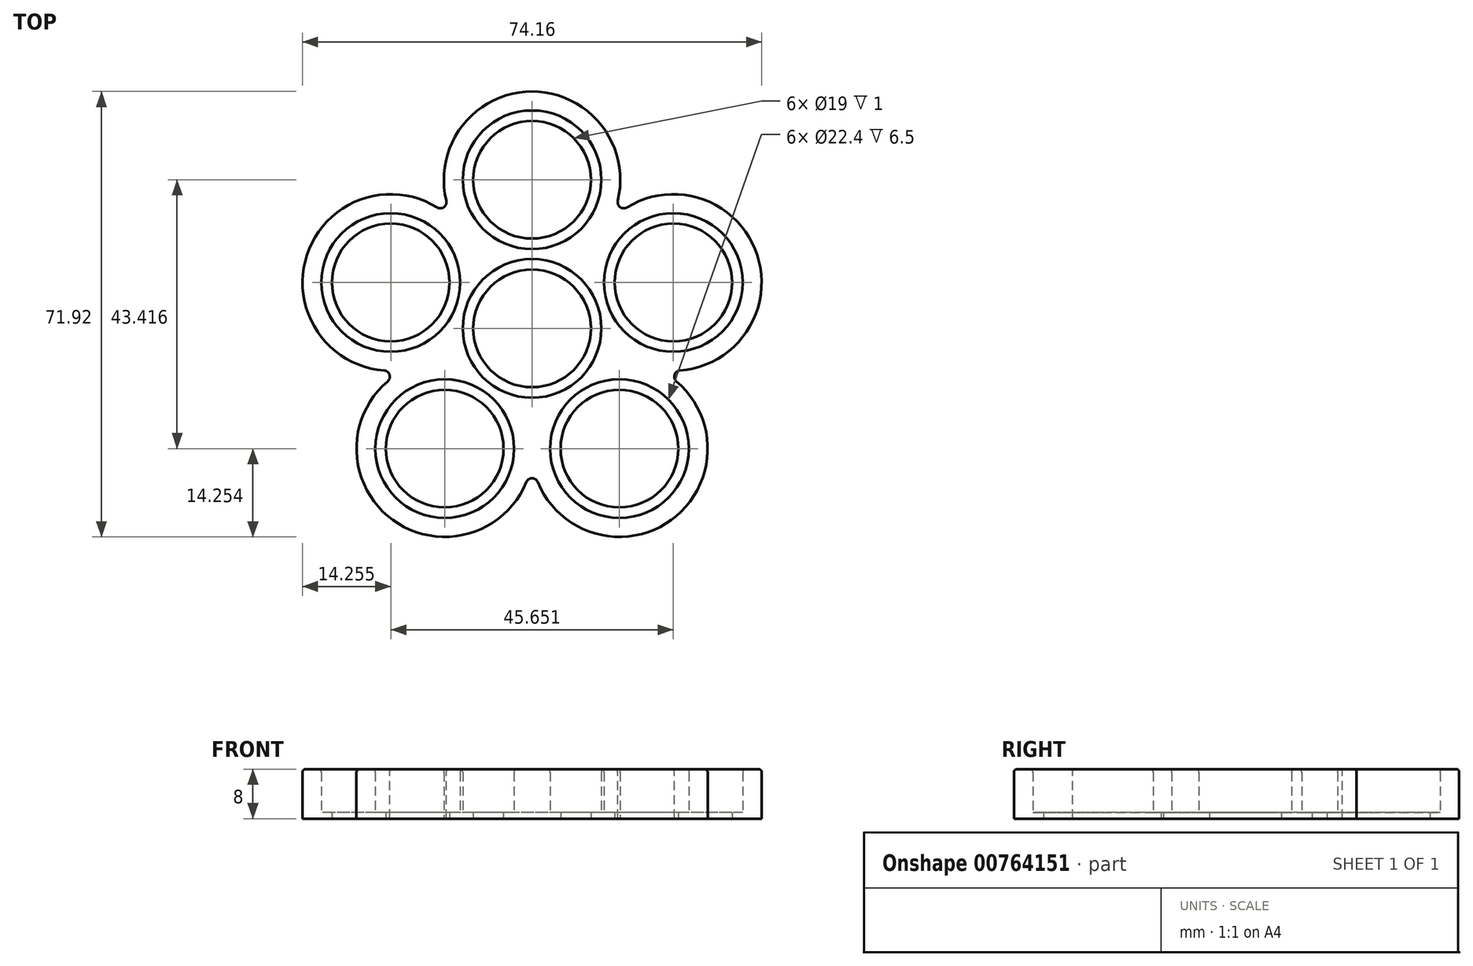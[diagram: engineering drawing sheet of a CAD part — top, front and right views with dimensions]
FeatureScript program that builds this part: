
annotation { "Feature Type Name" : "Feature", "Feature Type Description" : "" }
export const myFeature = defineFeature(function(context is Context, id is Id, definition is map)
    precondition{}
    {
        {
            var Q0;
            Q0=qCreatedBy(makeId("Top.planeOp"),FACE);
            var sketch = newSketch(context, id + "F0", { "sketchPlane" : qUnion([Q0])});
            skCircle(sketch, "E0", {"center": v(0, 0) * mm, "radius": 11.2 * mm});
            skCircle(sketch, "E1", {"center": v(0, 0) * mm, "radius": 14 * mm});
            skCircle(sketch, "E2", {"center": v(0, 24) * mm, "radius": 11.2 * mm});
            skCircle(sketch, "E3", {"center": v(0, 24) * mm, "radius": 14.25 * mm});
            skLineSegment(sketch, "E4", {"start": v(0, 24) * mm, "end": v(0, 0) * mm, "construction": true});
            skCircle(sketch, "E5", {"center": v(0, 24) * mm, "radius": 9.5 * mm});
            skCircle(sketch, "E6", {"center": v(0, 0) * mm, "radius": 9.5 * mm});
            skLineSegment(sketch, "E7.1.0", {"start": v(-22.83, 7.42) * mm, "end": v(0, 0) * mm, "construction": true});
            skCircle(sketch, "E7.1.1", {"center": v(-22.83, 7.42) * mm, "radius": 9.5 * mm});
            skCircle(sketch, "E7.1.2", {"center": v(-22.83, 7.42) * mm, "radius": 11.2 * mm});
            skCircle(sketch, "E7.1.3", {"center": v(-22.83, 7.42) * mm, "radius": 14.25 * mm});
            skLineSegment(sketch, "E7.2.0", {"start": v(-14.1, -19.42) * mm, "end": v(0, 0) * mm, "construction": true});
            skCircle(sketch, "E7.2.1", {"center": v(-14.1, -19.42) * mm, "radius": 9.5 * mm});
            skCircle(sketch, "E7.2.2", {"center": v(-14.1, -19.42) * mm, "radius": 11.2 * mm});
            skCircle(sketch, "E7.2.3", {"center": v(-14.1, -19.42) * mm, "radius": 14.25 * mm});
            skLineSegment(sketch, "E7.3.0", {"start": v(14.1, -19.42) * mm, "end": v(0, 0) * mm, "construction": true});
            skCircle(sketch, "E7.3.1", {"center": v(14.1, -19.42) * mm, "radius": 9.5 * mm});
            skCircle(sketch, "E7.3.2", {"center": v(14.1, -19.42) * mm, "radius": 11.2 * mm});
            skCircle(sketch, "E7.3.3", {"center": v(14.1, -19.42) * mm, "radius": 14.25 * mm});
            skLineSegment(sketch, "E7.4.0", {"start": v(22.83, 7.42) * mm, "end": v(0, 0) * mm, "construction": true});
            skCircle(sketch, "E7.4.1", {"center": v(22.83, 7.42) * mm, "radius": 9.5 * mm});
            skCircle(sketch, "E7.4.2", {"center": v(22.83, 7.42) * mm, "radius": 11.2 * mm});
            skCircle(sketch, "E7.4.3", {"center": v(22.83, 7.42) * mm, "radius": 14.25 * mm});
            skSolve(sketch);
        }
        {
            var Q0;
            Q0=qSketchRegion(id+"F0",true);
            var Q1;
            Q1=makeQuery(id+"F0.imprint","IMPRINT",FACE,{"disambiguationData":[TD([[makeQuery(id+"F0.imprint","IMPRINT",EDGE,{"derivedFrom":sQuery(id+"F0.wireOp",EDGE,"E0")}),1.0]])]});
            var Q2;
            {var subQ0=sQuery(id+"F0.wireOp",EDGE,"E2");var subQ1=sQuery(id+"F0.wireOp",EDGE,"E1");var subQ2=makeQuery(id+"F0.imprint","INTERSECT",VERTEX,{"disambiguationData":[OD(0.0)],"derivedFrom":[subQ1,subQ0]});Q2=makeQuery(id+"F0.imprint","IMPRINT",FACE,{"disambiguationData":[TD([[makeQuery(id+"F0.imprint","IMPRINT",EDGE,{"disambiguationData":[TD([[subQ2,-1.0]])],"derivedFrom":subQ1}),1.0]])]});}
            var Q3;
            {var subQ0=sQuery(id+"F0.wireOp",EDGE,"E2");var subQ1=sQuery(id+"F0.wireOp",EDGE,"E1");var subQ2=makeQuery(id+"F0.imprint","INTERSECT",VERTEX,{"disambiguationData":[OD(0.0)],"derivedFrom":[subQ1,subQ0]});Q3=makeQuery(id+"F0.imprint","IMPRINT",FACE,{"disambiguationData":[TD([[makeQuery(id+"F0.imprint","IMPRINT",EDGE,{"disambiguationData":[TD([[subQ2,-1.0]])],"derivedFrom":subQ1}),-1.0]])]});}
            var Q4;
            {var subQ0=sQuery(id+"F0.wireOp",EDGE,"MJdSrlI8-rVfH-V2LY-VGwR-c2a5gXK0sPas");var subQ1=sQuery(id+"F0.wireOp",EDGE,"E1");var subQ2=makeQuery(id+"F0.imprint","INTERSECT",VERTEX,{"disambiguationData":[OD(0.0)],"derivedFrom":[subQ1,subQ0]});Q4=makeQuery(id+"F0.imprint","IMPRINT",FACE,{"disambiguationData":[TD([[makeQuery(id+"F0.imprint","IMPRINT",EDGE,{"disambiguationData":[TD([[subQ2,-1.0]])],"derivedFrom":subQ1}),1.0]])]});}
            var Q5;
            {var subQ0=sQuery(id+"F0.wireOp",EDGE,"MJdSrlI8-rVfH-V2LY-VGwR-c2a5gXK0sPas");var subQ1=sQuery(id+"F0.wireOp",EDGE,"E1");var subQ2=makeQuery(id+"F0.imprint","INTERSECT",VERTEX,{"disambiguationData":[OD(0.0)],"derivedFrom":[subQ1,subQ0]});Q5=makeQuery(id+"F0.imprint","IMPRINT",FACE,{"disambiguationData":[TD([[makeQuery(id+"F0.imprint","IMPRINT",EDGE,{"disambiguationData":[TD([[subQ2,-1.0]])],"derivedFrom":subQ1}),-1.0]])]});}
            var Q6;
            {var subQ0=sQuery(id+"F0.wireOp",EDGE,"zHFCQELd-Fm6N-4mPB-3y46-Qqn4AbVFevso");var subQ1=sQuery(id+"F0.wireOp",EDGE,"E1");var subQ2=makeQuery(id+"F0.imprint","INTERSECT",VERTEX,{"disambiguationData":[OD(0.0)],"derivedFrom":[subQ1,subQ0]});Q6=makeQuery(id+"F0.imprint","IMPRINT",FACE,{"disambiguationData":[TD([[makeQuery(id+"F0.imprint","IMPRINT",EDGE,{"disambiguationData":[TD([[subQ2,-1.0]])],"derivedFrom":subQ1}),1.0]])]});}
            var Q7;
            {var subQ0=sQuery(id+"F0.wireOp",EDGE,"zHFCQELd-Fm6N-4mPB-3y46-Qqn4AbVFevso");var subQ1=sQuery(id+"F0.wireOp",EDGE,"E1");var subQ2=makeQuery(id+"F0.imprint","INTERSECT",VERTEX,{"disambiguationData":[OD(0.0)],"derivedFrom":[subQ1,subQ0]});Q7=makeQuery(id+"F0.imprint","IMPRINT",FACE,{"disambiguationData":[TD([[makeQuery(id+"F0.imprint","IMPRINT",EDGE,{"disambiguationData":[TD([[subQ2,-1.0]])],"derivedFrom":subQ1}),-1.0]])]});}
            var Q8;
            {var subQ0=sQuery(id+"F0.wireOp",EDGE,"owKKNgS1-acpY-2382-gatt-TBliOJCZXLt6");var subQ1=sQuery(id+"F0.wireOp",EDGE,"E0");var subQ2=makeQuery(id+"F0.imprint","INTERSECT",VERTEX,{"disambiguationData":[OD(0.0)],"derivedFrom":[subQ1,subQ0]});Q8=makeQuery(id+"F0.imprint","IMPRINT",FACE,{"disambiguationData":[TD([[makeQuery(id+"F0.imprint","IMPRINT",EDGE,{"disambiguationData":[TD([[subQ2,-1.0]])],"derivedFrom":subQ1}),1.0]])]});}
            var Q9;
            {var subQ0=sQuery(id+"F0.wireOp",EDGE,"aMbKunLI-uIGq-Xlfk-LzCX-02N4p1kP5Les");var subQ1=sQuery(id+"F0.wireOp",EDGE,"E0");var subQ2=makeQuery(id+"F0.imprint","INTERSECT",VERTEX,{"disambiguationData":[OD(0.0)],"derivedFrom":[subQ1,subQ0]});Q9=makeQuery(id+"F0.imprint","IMPRINT",FACE,{"disambiguationData":[TD([[makeQuery(id+"F0.imprint","IMPRINT",EDGE,{"disambiguationData":[TD([[subQ2,-1.0]])],"derivedFrom":subQ1}),1.0]])]});}
            var Q10;
            {var subQ0=sQuery(id+"F0.wireOp",EDGE,"E3");var subQ1=sQuery(id+"F0.wireOp",EDGE,"E0");var subQ2=makeQuery(id+"F0.imprint","INTERSECT",VERTEX,{"disambiguationData":[OD(0.0)],"derivedFrom":[subQ1,subQ0]});Q10=makeQuery(id+"F0.imprint","IMPRINT",FACE,{"disambiguationData":[TD([[makeQuery(id+"F0.imprint","IMPRINT",EDGE,{"disambiguationData":[TD([[subQ2,1.0]])],"derivedFrom":subQ1}),1.0]])]});}
            var Q11;
            {var subQ4=sQuery(id+"F0.wireOp",EDGE,"E3");var subQ7=sQuery(id+"F0.wireOp",EDGE,"E0");var subQ8=makeQuery(id+"F0.imprint","INTERSECT",VERTEX,{"disambiguationData":[OD(0.0)],"derivedFrom":[subQ7,subQ4]});Q11=makeQuery(id+"F0.imprint","IMPRINT",FACE,{"disambiguationData":[TD([[makeQuery(id+"F0.imprint","IMPRINT",EDGE,{"disambiguationData":[TD([[subQ8,-1.0]])],"derivedFrom":subQ7}),-1.0]])]});}
            var Q12;
            {var subQ0=sQuery(id+"F0.wireOp",EDGE,"E3");var subQ1=sQuery(id+"F0.wireOp",EDGE,"E0");var subQ2=makeQuery(id+"F0.imprint","INTERSECT",VERTEX,{"disambiguationData":[OD(0.0)],"derivedFrom":[subQ1,subQ0]});Q12=makeQuery(id+"F0.imprint","IMPRINT",FACE,{"disambiguationData":[TD([[makeQuery(id+"F0.imprint","IMPRINT",EDGE,{"disambiguationData":[TD([[subQ2,-1.0]])],"derivedFrom":subQ1}),1.0]])]});}
            var Q13;
            Q13=makeQuery(id+"F0.imprint","IMPRINT",FACE,{"disambiguationData":[TD([[makeQuery(id+"F0.imprint","IMPRINT",EDGE,{"derivedFrom":sQuery(id+"F0.wireOp",EDGE,"E7.1.1")}),-1.0]])]});
            var Q14;
            Q14=makeQuery(id+"F0.imprint","IMPRINT",FACE,{"disambiguationData":[TD([[makeQuery(id+"F0.imprint","IMPRINT",EDGE,{"derivedFrom":sQuery(id+"F0.wireOp",EDGE,"E7.4.1")}),-1.0]])]});
            var Q15;
            Q15=makeQuery(id+"F0.imprint","IMPRINT",FACE,{"disambiguationData":[TD([[makeQuery(id+"F0.imprint","IMPRINT",EDGE,{"derivedFrom":sQuery(id+"F0.wireOp",EDGE,"E7.3.1")}),-1.0]])]});
            var Q16;
            Q16=makeQuery(id+"F0.imprint","IMPRINT",FACE,{"disambiguationData":[TD([[makeQuery(id+"F0.imprint","IMPRINT",EDGE,{"derivedFrom":sQuery(id+"F0.wireOp",EDGE,"E7.2.1")}),-1.0]])]});
            var Q17;
            {var subQ0=sQuery(id+"F0.wireOp",EDGE,"E7.1.3");var subQ1=sQuery(id+"F0.wireOp",EDGE,"E1");var subQ2=makeQuery(id+"F0.imprint","INTERSECT",VERTEX,{"disambiguationData":[OD(1.0)],"derivedFrom":[subQ1,subQ0]});Q17=makeQuery(id+"F0.imprint","IMPRINT",FACE,{"disambiguationData":[TD([[makeQuery(id+"F0.imprint","IMPRINT",EDGE,{"disambiguationData":[TD([[subQ2,-1.0]])],"derivedFrom":subQ1}),-1.0]])]});}
            var Q18;
            {var subQ0=sQuery(id+"F0.wireOp",EDGE,"E7.1.3");var subQ1=sQuery(id+"F0.wireOp",EDGE,"E0");var subQ2=makeQuery(id+"F0.imprint","INTERSECT",VERTEX,{"disambiguationData":[OD(1.0)],"derivedFrom":[subQ1,subQ0]});Q18=makeQuery(id+"F0.imprint","IMPRINT",FACE,{"disambiguationData":[TD([[makeQuery(id+"F0.imprint","IMPRINT",EDGE,{"disambiguationData":[TD([[subQ2,-1.0]])],"derivedFrom":subQ1}),-1.0]])]});}
            var Q19;
            {var subQ4=sQuery(id+"F0.wireOp",EDGE,"E7.2.3");var subQ7=sQuery(id+"F0.wireOp",EDGE,"E0");var subQ8=makeQuery(id+"F0.imprint","INTERSECT",VERTEX,{"disambiguationData":[OD(0.0)],"derivedFrom":[subQ7,subQ4]});Q19=makeQuery(id+"F0.imprint","IMPRINT",FACE,{"disambiguationData":[TD([[makeQuery(id+"F0.imprint","IMPRINT",EDGE,{"disambiguationData":[TD([[subQ8,-1.0]])],"derivedFrom":subQ7}),-1.0]])]});}
            var Q20;
            {var subQ0=sQuery(id+"F0.wireOp",EDGE,"E7.2.2");var subQ1=sQuery(id+"F0.wireOp",EDGE,"E1");var subQ2=makeQuery(id+"F0.imprint","INTERSECT",VERTEX,{"disambiguationData":[OD(0.0)],"derivedFrom":[subQ1,subQ0]});Q20=makeQuery(id+"F0.imprint","IMPRINT",FACE,{"disambiguationData":[TD([[makeQuery(id+"F0.imprint","IMPRINT",EDGE,{"disambiguationData":[TD([[subQ2,-1.0]])],"derivedFrom":subQ1}),1.0]])]});}
            var Q21;
            {var subQ0=sQuery(id+"F0.wireOp",EDGE,"E7.2.3");var subQ1=sQuery(id+"F0.wireOp",EDGE,"E0");var subQ2=makeQuery(id+"F0.imprint","INTERSECT",VERTEX,{"disambiguationData":[OD(0.0)],"derivedFrom":[subQ1,subQ0]});Q21=makeQuery(id+"F0.imprint","IMPRINT",FACE,{"disambiguationData":[TD([[makeQuery(id+"F0.imprint","IMPRINT",EDGE,{"disambiguationData":[TD([[subQ2,-1.0]])],"derivedFrom":subQ1}),1.0]])]});}
            var Q22;
            {var subQ3=sQuery(id+"F0.wireOp",EDGE,"E7.1.3");var subQ7=sQuery(id+"F0.wireOp",EDGE,"E0");var subQ8=makeQuery(id+"F0.imprint","INTERSECT",VERTEX,{"disambiguationData":[OD(0.0)],"derivedFrom":[subQ7,subQ3]});Q22=makeQuery(id+"F0.imprint","IMPRINT",FACE,{"disambiguationData":[TD([[makeQuery(id+"F0.imprint","IMPRINT",EDGE,{"disambiguationData":[TD([[subQ8,-1.0]])],"derivedFrom":subQ7}),-1.0]])]});}
            var Q23;
            {var subQ0=sQuery(id+"F0.wireOp",EDGE,"E7.1.2");var subQ1=sQuery(id+"F0.wireOp",EDGE,"E1");var subQ2=makeQuery(id+"F0.imprint","INTERSECT",VERTEX,{"disambiguationData":[OD(0.0)],"derivedFrom":[subQ1,subQ0]});Q23=makeQuery(id+"F0.imprint","IMPRINT",FACE,{"disambiguationData":[TD([[makeQuery(id+"F0.imprint","IMPRINT",EDGE,{"disambiguationData":[TD([[subQ2,-1.0]])],"derivedFrom":subQ1}),1.0]])]});}
            var Q24;
            {var subQ0=sQuery(id+"F0.wireOp",EDGE,"E7.1.3");var subQ1=sQuery(id+"F0.wireOp",EDGE,"E0");var subQ2=makeQuery(id+"F0.imprint","INTERSECT",VERTEX,{"disambiguationData":[OD(0.0)],"derivedFrom":[subQ1,subQ0]});Q24=makeQuery(id+"F0.imprint","IMPRINT",FACE,{"disambiguationData":[TD([[makeQuery(id+"F0.imprint","IMPRINT",EDGE,{"disambiguationData":[TD([[subQ2,-1.0]])],"derivedFrom":subQ1}),1.0]])]});}
            var Q25;
            {var subQ0=sQuery(id+"F0.wireOp",EDGE,"E3");var subQ1=sQuery(id+"F0.wireOp",EDGE,"E0");var subQ2=makeQuery(id+"F0.imprint","INTERSECT",VERTEX,{"disambiguationData":[OD(1.0)],"derivedFrom":[subQ1,subQ0]});Q25=makeQuery(id+"F0.imprint","IMPRINT",FACE,{"disambiguationData":[TD([[makeQuery(id+"F0.imprint","IMPRINT",EDGE,{"disambiguationData":[TD([[subQ2,-1.0]])],"derivedFrom":subQ1}),-1.0]])]});}
            var Q26;
            {var subQ0=sQuery(id+"F0.wireOp",EDGE,"E3");var subQ1=sQuery(id+"F0.wireOp",EDGE,"E1");var subQ2=makeQuery(id+"F0.imprint","INTERSECT",VERTEX,{"disambiguationData":[OD(1.0)],"derivedFrom":[subQ1,subQ0]});Q26=makeQuery(id+"F0.imprint","IMPRINT",FACE,{"disambiguationData":[TD([[makeQuery(id+"F0.imprint","IMPRINT",EDGE,{"disambiguationData":[TD([[subQ2,-1.0]])],"derivedFrom":subQ1}),-1.0]])]});}
            var Q27;
            {var subQ0=sQuery(id+"F0.wireOp",EDGE,"E3");var subQ1=sQuery(id+"F0.wireOp",EDGE,"E0");var subQ2=makeQuery(id+"F0.imprint","INTERSECT",VERTEX,{"disambiguationData":[OD(0.0)],"derivedFrom":[subQ1,subQ0]});Q27=makeQuery(id+"F0.imprint","IMPRINT",FACE,{"disambiguationData":[TD([[makeQuery(id+"F0.imprint","IMPRINT",EDGE,{"disambiguationData":[TD([[subQ2,1.0]])],"derivedFrom":subQ1}),-1.0]])]});}
            var Q28;
            {var subQ0=sQuery(id+"F0.wireOp",EDGE,"E7.4.3");var subQ1=sQuery(id+"F0.wireOp",EDGE,"E1");var subQ2=makeQuery(id+"F0.imprint","INTERSECT",VERTEX,{"disambiguationData":[OD(0.0)],"derivedFrom":[subQ1,subQ0]});Q28=makeQuery(id+"F0.imprint","IMPRINT",FACE,{"disambiguationData":[TD([[makeQuery(id+"F0.imprint","IMPRINT",EDGE,{"disambiguationData":[TD([[subQ2,-1.0]])],"derivedFrom":subQ1}),-1.0]])]});}
            var Q29;
            {var subQ4=sQuery(id+"F0.wireOp",EDGE,"E7.4.3");var subQ7=sQuery(id+"F0.wireOp",EDGE,"E0");var subQ8=makeQuery(id+"F0.imprint","INTERSECT",VERTEX,{"disambiguationData":[OD(0.0)],"derivedFrom":[subQ7,subQ4]});Q29=makeQuery(id+"F0.imprint","IMPRINT",FACE,{"disambiguationData":[TD([[makeQuery(id+"F0.imprint","IMPRINT",EDGE,{"disambiguationData":[TD([[subQ8,1.0]])],"derivedFrom":subQ7}),-1.0]])]});}
            var Q30;
            {var subQ0=sQuery(id+"F0.wireOp",EDGE,"E7.4.2");var subQ1=sQuery(id+"F0.wireOp",EDGE,"E1");var subQ2=makeQuery(id+"F0.imprint","INTERSECT",VERTEX,{"disambiguationData":[OD(0.0)],"derivedFrom":[subQ1,subQ0]});Q30=makeQuery(id+"F0.imprint","IMPRINT",FACE,{"disambiguationData":[TD([[makeQuery(id+"F0.imprint","IMPRINT",EDGE,{"disambiguationData":[TD([[subQ2,1.0]])],"derivedFrom":subQ1}),1.0]])]});}
            var Q31;
            {var subQ0=sQuery(id+"F0.wireOp",EDGE,"E7.4.3");var subQ1=sQuery(id+"F0.wireOp",EDGE,"E0");var subQ2=makeQuery(id+"F0.imprint","INTERSECT",VERTEX,{"disambiguationData":[OD(0.0)],"derivedFrom":[subQ1,subQ0]});Q31=makeQuery(id+"F0.imprint","IMPRINT",FACE,{"disambiguationData":[TD([[makeQuery(id+"F0.imprint","IMPRINT",EDGE,{"disambiguationData":[TD([[subQ2,1.0]])],"derivedFrom":subQ1}),1.0]])]});}
            var Q32;
            {var subQ0=sQuery(id+"F0.wireOp",EDGE,"E7.3.3");var subQ1=sQuery(id+"F0.wireOp",EDGE,"E1");var subQ2=makeQuery(id+"F0.imprint","INTERSECT",VERTEX,{"disambiguationData":[OD(1.0)],"derivedFrom":[subQ1,subQ0]});Q32=makeQuery(id+"F0.imprint","IMPRINT",FACE,{"disambiguationData":[TD([[makeQuery(id+"F0.imprint","IMPRINT",EDGE,{"disambiguationData":[TD([[subQ2,-1.0]])],"derivedFrom":subQ1}),-1.0]])]});}
            var Q33;
            {var subQ0=sQuery(id+"F0.wireOp",EDGE,"E7.3.3");var subQ1=sQuery(id+"F0.wireOp",EDGE,"E0");var subQ2=makeQuery(id+"F0.imprint","INTERSECT",VERTEX,{"disambiguationData":[OD(1.0)],"derivedFrom":[subQ1,subQ0]});Q33=makeQuery(id+"F0.imprint","IMPRINT",FACE,{"disambiguationData":[TD([[makeQuery(id+"F0.imprint","IMPRINT",EDGE,{"disambiguationData":[TD([[subQ2,-1.0]])],"derivedFrom":subQ1}),-1.0]])]});}
            var Q34;
            {var subQ4=sQuery(id+"F0.wireOp",EDGE,"E7.3.3");var subQ6=sQuery(id+"F0.wireOp",EDGE,"E0");var subQ9=makeQuery(id+"F0.imprint","INTERSECT",VERTEX,{"disambiguationData":[OD(0.0)],"derivedFrom":[subQ6,subQ4]});Q34=makeQuery(id+"F0.imprint","IMPRINT",FACE,{"disambiguationData":[TD([[makeQuery(id+"F0.imprint","IMPRINT",EDGE,{"disambiguationData":[TD([[subQ9,-1.0]])],"derivedFrom":subQ6}),-1.0]])]});}
            var Q35;
            {var subQ0=sQuery(id+"F0.wireOp",EDGE,"E7.3.3");var subQ1=sQuery(id+"F0.wireOp",EDGE,"E0");var subQ2=makeQuery(id+"F0.imprint","INTERSECT",VERTEX,{"disambiguationData":[OD(0.0)],"derivedFrom":[subQ1,subQ0]});Q35=makeQuery(id+"F0.imprint","IMPRINT",FACE,{"disambiguationData":[TD([[makeQuery(id+"F0.imprint","IMPRINT",EDGE,{"disambiguationData":[TD([[subQ2,-1.0]])],"derivedFrom":subQ1}),1.0]])]});}
            var Q36;
            {var subQ0=sQuery(id+"F0.wireOp",EDGE,"E7.3.2");var subQ1=sQuery(id+"F0.wireOp",EDGE,"E1");var subQ2=makeQuery(id+"F0.imprint","INTERSECT",VERTEX,{"disambiguationData":[OD(0.0)],"derivedFrom":[subQ1,subQ0]});Q36=makeQuery(id+"F0.imprint","IMPRINT",FACE,{"disambiguationData":[TD([[makeQuery(id+"F0.imprint","IMPRINT",EDGE,{"disambiguationData":[TD([[subQ2,-1.0]])],"derivedFrom":subQ1}),1.0]])]});}
            var Q37;
            {var subQ0=sQuery(id+"F0.wireOp",EDGE,"E7.2.3");var subQ1=sQuery(id+"F0.wireOp",EDGE,"E0");var subQ2=makeQuery(id+"F0.imprint","INTERSECT",VERTEX,{"disambiguationData":[OD(1.0)],"derivedFrom":[subQ1,subQ0]});Q37=makeQuery(id+"F0.imprint","IMPRINT",FACE,{"disambiguationData":[TD([[makeQuery(id+"F0.imprint","IMPRINT",EDGE,{"disambiguationData":[TD([[subQ2,-1.0]])],"derivedFrom":subQ1}),-1.0]])]});}
            var Q38;
            {var subQ0=sQuery(id+"F0.wireOp",EDGE,"E7.2.3");var subQ1=sQuery(id+"F0.wireOp",EDGE,"E1");var subQ2=makeQuery(id+"F0.imprint","INTERSECT",VERTEX,{"disambiguationData":[OD(1.0)],"derivedFrom":[subQ1,subQ0]});Q38=makeQuery(id+"F0.imprint","IMPRINT",FACE,{"disambiguationData":[TD([[makeQuery(id+"F0.imprint","IMPRINT",EDGE,{"disambiguationData":[TD([[subQ2,-1.0]])],"derivedFrom":subQ1}),-1.0]])]});}
            extrude(context, id + "F1", {"entities" : qUnion([Q0, Q1, Q2, Q3, Q4, Q5, Q6, Q7, Q8, Q9, Q10, Q11, Q12, Q13, Q14, Q15, Q16, Q17, Q18, Q19, Q20, Q21, Q22, Q23, Q24, Q25, Q26, Q27, Q28, Q29, Q30, Q31, Q32, Q33, Q34, Q35, Q36, Q37, Q38]), "depth" : 1 * mm, "offsetDistance" : 25 * mm});
        }
        {
            var Q0;
            {var subQ0=sQuery(id+"F0.wireOp",EDGE,"E7.4.3");var subQ1=sQuery(id+"F0.wireOp",EDGE,"E1");var subQ2=makeQuery(id+"F0.imprint","INTERSECT",VERTEX,{"disambiguationData":[OD(0.0)],"derivedFrom":[subQ1,subQ0]});Q0=makeQuery(id+"F0.imprint","IMPRINT",FACE,{"disambiguationData":[TD([[makeQuery(id+"F0.imprint","IMPRINT",EDGE,{"disambiguationData":[TD([[subQ2,-1.0]])],"derivedFrom":subQ1}),-1.0]])]});}
            var Q1;
            {var subQ7=sQuery(id+"F0.wireOp",EDGE,"E7.4.2");var subQ8=sQuery(id+"F0.wireOp",EDGE,"E1");var subQ11=makeQuery(id+"F0.imprint","INTERSECT",VERTEX,{"disambiguationData":[OD(0.0)],"derivedFrom":[subQ8,subQ7]});Q1=makeQuery(id+"F0.imprint","IMPRINT",FACE,{"disambiguationData":[TD([[makeQuery(id+"F0.imprint","IMPRINT",EDGE,{"disambiguationData":[TD([[subQ11,-1.0]])],"derivedFrom":subQ8}),-1.0]])]});}
            var Q2;
            {var subQ4=sQuery(id+"F0.wireOp",EDGE,"E7.4.3");var subQ7=sQuery(id+"F0.wireOp",EDGE,"E0");var subQ8=makeQuery(id+"F0.imprint","INTERSECT",VERTEX,{"disambiguationData":[OD(0.0)],"derivedFrom":[subQ7,subQ4]});Q2=makeQuery(id+"F0.imprint","IMPRINT",FACE,{"disambiguationData":[TD([[makeQuery(id+"F0.imprint","IMPRINT",EDGE,{"disambiguationData":[TD([[subQ8,1.0]])],"derivedFrom":subQ7}),-1.0]])]});}
            var Q3;
            {var subQ0=sQuery(id+"F0.wireOp",EDGE,"E3");var subQ1=sQuery(id+"F0.wireOp",EDGE,"E0");var subQ2=makeQuery(id+"F0.imprint","INTERSECT",VERTEX,{"disambiguationData":[OD(0.0)],"derivedFrom":[subQ1,subQ0]});Q3=makeQuery(id+"F0.imprint","IMPRINT",FACE,{"disambiguationData":[TD([[makeQuery(id+"F0.imprint","IMPRINT",EDGE,{"disambiguationData":[TD([[subQ2,1.0]])],"derivedFrom":subQ1}),-1.0]])]});}
            var Q4;
            {var subQ4=sQuery(id+"F0.wireOp",EDGE,"E3");var subQ7=sQuery(id+"F0.wireOp",EDGE,"E0");var subQ8=makeQuery(id+"F0.imprint","INTERSECT",VERTEX,{"disambiguationData":[OD(0.0)],"derivedFrom":[subQ7,subQ4]});Q4=makeQuery(id+"F0.imprint","IMPRINT",FACE,{"disambiguationData":[TD([[makeQuery(id+"F0.imprint","IMPRINT",EDGE,{"disambiguationData":[TD([[subQ8,-1.0]])],"derivedFrom":subQ7}),-1.0]])]});}
            var Q5;
            {var subQ1=sQuery(id+"F0.wireOp",EDGE,"E1");var subQ4=sQuery(id+"F0.wireOp",EDGE,"E3");var subQ6=makeQuery(id+"F0.imprint","INTERSECT",VERTEX,{"disambiguationData":[OD(0.0)],"derivedFrom":[subQ1,subQ4]});Q5=makeQuery(id+"F0.imprint","IMPRINT",FACE,{"disambiguationData":[TD([[makeQuery(id+"F0.imprint","IMPRINT",EDGE,{"disambiguationData":[TD([[subQ6,-1.0]])],"derivedFrom":subQ1}),-1.0]])]});}
            var Q6;
            {var subQ1=sQuery(id+"F0.wireOp",EDGE,"E1");var subQ4=sQuery(id+"F0.wireOp",EDGE,"E7.1.3");var subQ11=makeQuery(id+"F0.imprint","INTERSECT",VERTEX,{"disambiguationData":[OD(0.0)],"derivedFrom":[subQ1,subQ4]});Q6=makeQuery(id+"F0.imprint","IMPRINT",FACE,{"disambiguationData":[TD([[makeQuery(id+"F0.imprint","IMPRINT",EDGE,{"disambiguationData":[TD([[subQ11,-1.0]])],"derivedFrom":subQ1}),-1.0]])]});}
            var Q7;
            {var subQ0=sQuery(id+"F0.wireOp",EDGE,"E3");var subQ1=sQuery(id+"F0.wireOp",EDGE,"E0");var subQ2=makeQuery(id+"F0.imprint","INTERSECT",VERTEX,{"disambiguationData":[OD(1.0)],"derivedFrom":[subQ1,subQ0]});Q7=makeQuery(id+"F0.imprint","IMPRINT",FACE,{"disambiguationData":[TD([[makeQuery(id+"F0.imprint","IMPRINT",EDGE,{"disambiguationData":[TD([[subQ2,-1.0]])],"derivedFrom":subQ1}),-1.0]])]});}
            var Q8;
            {var subQ3=sQuery(id+"F0.wireOp",EDGE,"E7.1.3");var subQ7=sQuery(id+"F0.wireOp",EDGE,"E0");var subQ8=makeQuery(id+"F0.imprint","INTERSECT",VERTEX,{"disambiguationData":[OD(0.0)],"derivedFrom":[subQ7,subQ3]});Q8=makeQuery(id+"F0.imprint","IMPRINT",FACE,{"disambiguationData":[TD([[makeQuery(id+"F0.imprint","IMPRINT",EDGE,{"disambiguationData":[TD([[subQ8,-1.0]])],"derivedFrom":subQ7}),-1.0]])]});}
            var Q9;
            {var subQ0=sQuery(id+"F0.wireOp",EDGE,"E7.1.3");var subQ1=sQuery(id+"F0.wireOp",EDGE,"E0");var subQ2=makeQuery(id+"F0.imprint","INTERSECT",VERTEX,{"disambiguationData":[OD(1.0)],"derivedFrom":[subQ1,subQ0]});Q9=makeQuery(id+"F0.imprint","IMPRINT",FACE,{"disambiguationData":[TD([[makeQuery(id+"F0.imprint","IMPRINT",EDGE,{"disambiguationData":[TD([[subQ2,-1.0]])],"derivedFrom":subQ1}),-1.0]])]});}
            var Q10;
            {var subQ4=sQuery(id+"F0.wireOp",EDGE,"E7.2.3");var subQ7=sQuery(id+"F0.wireOp",EDGE,"E0");var subQ8=makeQuery(id+"F0.imprint","INTERSECT",VERTEX,{"disambiguationData":[OD(0.0)],"derivedFrom":[subQ7,subQ4]});Q10=makeQuery(id+"F0.imprint","IMPRINT",FACE,{"disambiguationData":[TD([[makeQuery(id+"F0.imprint","IMPRINT",EDGE,{"disambiguationData":[TD([[subQ8,-1.0]])],"derivedFrom":subQ7}),-1.0]])]});}
            var Q11;
            {var subQ1=sQuery(id+"F0.wireOp",EDGE,"E1");var subQ4=sQuery(id+"F0.wireOp",EDGE,"E7.2.3");var subQ9=makeQuery(id+"F0.imprint","INTERSECT",VERTEX,{"disambiguationData":[OD(0.0)],"derivedFrom":[subQ1,subQ4]});Q11=makeQuery(id+"F0.imprint","IMPRINT",FACE,{"disambiguationData":[TD([[makeQuery(id+"F0.imprint","IMPRINT",EDGE,{"disambiguationData":[TD([[subQ9,-1.0]])],"derivedFrom":subQ1}),-1.0]])]});}
            var Q12;
            {var subQ1=sQuery(id+"F0.wireOp",EDGE,"E1");var subQ4=sQuery(id+"F0.wireOp",EDGE,"E7.3.3");var subQ9=makeQuery(id+"F0.imprint","INTERSECT",VERTEX,{"disambiguationData":[OD(0.0)],"derivedFrom":[subQ1,subQ4]});Q12=makeQuery(id+"F0.imprint","IMPRINT",FACE,{"disambiguationData":[TD([[makeQuery(id+"F0.imprint","IMPRINT",EDGE,{"disambiguationData":[TD([[subQ9,-1.0]])],"derivedFrom":subQ1}),-1.0]])]});}
            var Q13;
            {var subQ0=sQuery(id+"F0.wireOp",EDGE,"E7.2.3");var subQ1=sQuery(id+"F0.wireOp",EDGE,"E1");var subQ2=makeQuery(id+"F0.imprint","INTERSECT",VERTEX,{"disambiguationData":[OD(1.0)],"derivedFrom":[subQ1,subQ0]});Q13=makeQuery(id+"F0.imprint","IMPRINT",FACE,{"disambiguationData":[TD([[makeQuery(id+"F0.imprint","IMPRINT",EDGE,{"disambiguationData":[TD([[subQ2,-1.0]])],"derivedFrom":subQ1}),-1.0]])]});}
            var Q14;
            {var subQ0=sQuery(id+"F0.wireOp",EDGE,"E7.2.3");var subQ1=sQuery(id+"F0.wireOp",EDGE,"E0");var subQ2=makeQuery(id+"F0.imprint","INTERSECT",VERTEX,{"disambiguationData":[OD(1.0)],"derivedFrom":[subQ1,subQ0]});Q14=makeQuery(id+"F0.imprint","IMPRINT",FACE,{"disambiguationData":[TD([[makeQuery(id+"F0.imprint","IMPRINT",EDGE,{"disambiguationData":[TD([[subQ2,-1.0]])],"derivedFrom":subQ1}),-1.0]])]});}
            var Q15;
            {var subQ0=sQuery(id+"F0.wireOp",EDGE,"E7.1.3");var subQ1=sQuery(id+"F0.wireOp",EDGE,"E1");var subQ2=makeQuery(id+"F0.imprint","INTERSECT",VERTEX,{"disambiguationData":[OD(1.0)],"derivedFrom":[subQ1,subQ0]});Q15=makeQuery(id+"F0.imprint","IMPRINT",FACE,{"disambiguationData":[TD([[makeQuery(id+"F0.imprint","IMPRINT",EDGE,{"disambiguationData":[TD([[subQ2,-1.0]])],"derivedFrom":subQ1}),-1.0]])]});}
            var Q16;
            {var subQ0=sQuery(id+"F0.wireOp",EDGE,"E3");var subQ1=sQuery(id+"F0.wireOp",EDGE,"E1");var subQ2=makeQuery(id+"F0.imprint","INTERSECT",VERTEX,{"disambiguationData":[OD(1.0)],"derivedFrom":[subQ1,subQ0]});Q16=makeQuery(id+"F0.imprint","IMPRINT",FACE,{"disambiguationData":[TD([[makeQuery(id+"F0.imprint","IMPRINT",EDGE,{"disambiguationData":[TD([[subQ2,-1.0]])],"derivedFrom":subQ1}),-1.0]])]});}
            var Q17;
            {var subQ0=sQuery(id+"F0.wireOp",EDGE,"E7.3.3");var subQ1=sQuery(id+"F0.wireOp",EDGE,"E1");var subQ2=makeQuery(id+"F0.imprint","INTERSECT",VERTEX,{"disambiguationData":[OD(1.0)],"derivedFrom":[subQ1,subQ0]});Q17=makeQuery(id+"F0.imprint","IMPRINT",FACE,{"disambiguationData":[TD([[makeQuery(id+"F0.imprint","IMPRINT",EDGE,{"disambiguationData":[TD([[subQ2,-1.0]])],"derivedFrom":subQ1}),-1.0]])]});}
            var Q18;
            {var subQ0=sQuery(id+"F0.wireOp",EDGE,"E7.3.3");var subQ1=sQuery(id+"F0.wireOp",EDGE,"E0");var subQ2=makeQuery(id+"F0.imprint","INTERSECT",VERTEX,{"disambiguationData":[OD(1.0)],"derivedFrom":[subQ1,subQ0]});Q18=makeQuery(id+"F0.imprint","IMPRINT",FACE,{"disambiguationData":[TD([[makeQuery(id+"F0.imprint","IMPRINT",EDGE,{"disambiguationData":[TD([[subQ2,-1.0]])],"derivedFrom":subQ1}),-1.0]])]});}
            var Q19;
            {var subQ4=sQuery(id+"F0.wireOp",EDGE,"E7.3.3");var subQ6=sQuery(id+"F0.wireOp",EDGE,"E0");var subQ9=makeQuery(id+"F0.imprint","INTERSECT",VERTEX,{"disambiguationData":[OD(0.0)],"derivedFrom":[subQ6,subQ4]});Q19=makeQuery(id+"F0.imprint","IMPRINT",FACE,{"disambiguationData":[TD([[makeQuery(id+"F0.imprint","IMPRINT",EDGE,{"disambiguationData":[TD([[subQ9,-1.0]])],"derivedFrom":subQ6}),-1.0]])]});}
            var Q20;
            {var subQ0=sQuery(id+"F0.wireOp",EDGE,"E7.3.3");var subQ1=sQuery(id+"F0.wireOp",EDGE,"E7.2.3");var subQ2=makeQuery(id+"F0.imprint","INTERSECT",VERTEX,{"disambiguationData":[OD(0.0)],"derivedFrom":[subQ1,subQ0]});Q20=makeQuery(id+"F0.imprint","IMPRINT",FACE,{"disambiguationData":[TD([[makeQuery(id+"F0.imprint","IMPRINT",EDGE,{"disambiguationData":[TD([[subQ2,-1.0]])],"derivedFrom":subQ1}),1.0]])]});}
            var Q21;
            {var subQ0=sQuery(id+"F0.wireOp",EDGE,"E7.2.3");var subQ1=sQuery(id+"F0.wireOp",EDGE,"E7.1.3");var subQ2=makeQuery(id+"F0.imprint","INTERSECT",VERTEX,{"disambiguationData":[OD(0.0)],"derivedFrom":[subQ1,subQ0]});Q21=makeQuery(id+"F0.imprint","IMPRINT",FACE,{"disambiguationData":[TD([[makeQuery(id+"F0.imprint","IMPRINT",EDGE,{"disambiguationData":[TD([[subQ2,-1.0]])],"derivedFrom":subQ1}),1.0]])]});}
            var Q22;
            {var subQ0=sQuery(id+"F0.wireOp",EDGE,"E7.1.3");var subQ1=sQuery(id+"F0.wireOp",EDGE,"E3");var subQ2=makeQuery(id+"F0.imprint","INTERSECT",VERTEX,{"disambiguationData":[OD(0.0)],"derivedFrom":[subQ1,subQ0]});Q22=makeQuery(id+"F0.imprint","IMPRINT",FACE,{"disambiguationData":[TD([[makeQuery(id+"F0.imprint","IMPRINT",EDGE,{"disambiguationData":[TD([[subQ2,-1.0]])],"derivedFrom":subQ1}),1.0]])]});}
            var Q23;
            {var subQ0=sQuery(id+"F0.wireOp",EDGE,"E7.4.3");var subQ1=sQuery(id+"F0.wireOp",EDGE,"E3");var subQ2=makeQuery(id+"F0.imprint","INTERSECT",VERTEX,{"disambiguationData":[OD(0.0)],"derivedFrom":[subQ1,subQ0]});Q23=makeQuery(id+"F0.imprint","IMPRINT",FACE,{"disambiguationData":[TD([[makeQuery(id+"F0.imprint","IMPRINT",EDGE,{"disambiguationData":[TD([[subQ2,1.0]])],"derivedFrom":subQ1}),1.0]])]});}
            var Q24;
            {var subQ0=sQuery(id+"F0.wireOp",EDGE,"E7.4.3");var subQ1=sQuery(id+"F0.wireOp",EDGE,"E7.3.3");var subQ2=makeQuery(id+"F0.imprint","INTERSECT",VERTEX,{"disambiguationData":[OD(0.0)],"derivedFrom":[subQ1,subQ0]});Q24=makeQuery(id+"F0.imprint","IMPRINT",FACE,{"disambiguationData":[TD([[makeQuery(id+"F0.imprint","IMPRINT",EDGE,{"disambiguationData":[TD([[subQ2,-1.0]])],"derivedFrom":subQ1}),1.0]])]});}
            extrude(context, id + "F2", {"entities" : qUnion([Q0, Q1, Q2, Q3, Q4, Q5, Q6, Q7, Q8, Q9, Q10, Q11, Q12, Q13, Q14, Q15, Q16, Q17, Q18, Q19, Q20, Q21, Q22, Q23, Q24]), "operationType" : NewBodyOperationType.ADD, "depth" : 8 * mm, "offsetDistance" : 25 * mm});
        }
        {
            var Q0;
            {var subQ0=sQuery(id+"F0.wireOp",EDGE,"E7.2.3");var subQ1=sQuery(id+"F0.wireOp",EDGE,"E7.1.3");Q0=makeQuery(id+"F2.boolean.opBoolean","MERGE",EDGE,{"derivedFrom":[makeQuery(id+"F1.opExtrude","SWEPT_EDGE",EDGE,{"disambiguationData":[OSD([subQ1,subQ0])]}),makeQuery(id+"F2.opExtrude","SWEPT_EDGE",EDGE,{"disambiguationData":[OSD([subQ1,subQ0])]})]});}
            var Q1;
            {var subQ0=sQuery(id+"F0.wireOp",EDGE,"E7.1.3");var subQ1=sQuery(id+"F0.wireOp",EDGE,"E3");Q1=makeQuery(id+"F2.boolean.opBoolean","MERGE",EDGE,{"derivedFrom":[makeQuery(id+"F1.opExtrude","SWEPT_EDGE",EDGE,{"disambiguationData":[OSD([subQ1,subQ0])]}),makeQuery(id+"F2.opExtrude","SWEPT_EDGE",EDGE,{"disambiguationData":[OSD([subQ1,subQ0])]})]});}
            var Q2;
            {var subQ0=sQuery(id+"F0.wireOp",EDGE,"E7.4.3");var subQ1=sQuery(id+"F0.wireOp",EDGE,"E3");Q2=makeQuery(id+"F2.boolean.opBoolean","MERGE",EDGE,{"derivedFrom":[makeQuery(id+"F1.opExtrude","SWEPT_EDGE",EDGE,{"disambiguationData":[OSD([subQ1,subQ0])]}),makeQuery(id+"F2.opExtrude","SWEPT_EDGE",EDGE,{"disambiguationData":[OSD([subQ1,subQ0])]})]});}
            var Q3;
            {var subQ0=sQuery(id+"F0.wireOp",EDGE,"E7.4.3");var subQ1=sQuery(id+"F0.wireOp",EDGE,"E7.3.3");Q3=makeQuery(id+"F2.boolean.opBoolean","MERGE",EDGE,{"derivedFrom":[makeQuery(id+"F1.opExtrude","SWEPT_EDGE",EDGE,{"disambiguationData":[OSD([subQ1,subQ0])]}),makeQuery(id+"F2.opExtrude","SWEPT_EDGE",EDGE,{"disambiguationData":[OSD([subQ1,subQ0])]})]});}
            var Q4;
            {var subQ0=sQuery(id+"F0.wireOp",EDGE,"E7.3.3");var subQ1=sQuery(id+"F0.wireOp",EDGE,"E7.2.3");Q4=makeQuery(id+"F2.boolean.opBoolean","MERGE",EDGE,{"derivedFrom":[makeQuery(id+"F1.opExtrude","SWEPT_EDGE",EDGE,{"disambiguationData":[OSD([subQ1,subQ0])]}),makeQuery(id+"F2.opExtrude","SWEPT_EDGE",EDGE,{"disambiguationData":[OSD([subQ1,subQ0])]})]});}
            fillet(context, id + "F3", {"entities" : qUnion([Q0, Q1, Q2, Q3, Q4]), "radius" : 1 * mm, "tangentPropagation" : true, "allowEdgeOverflow" : false});
        }
        {
            var Q0;
            Q0=makeQuery(id+"F2.opExtrude","CAP_EDGE",EDGE,{"disambiguationData":[OSD([sQuery(id+"F0.wireOp",EDGE,"E7.4.3")])],"isStart":false});
            var Q1;
            Q1=makeQuery(id+"F2.opExtrude","CAP_EDGE",EDGE,{"disambiguationData":[OSD([sQuery(id+"F0.wireOp",EDGE,"E0")])],"isStart":false});
            var Q2;
            Q2=makeQuery(id+"F2.opExtrude","CAP_EDGE",EDGE,{"disambiguationData":[OSD([sQuery(id+"F0.wireOp",EDGE,"E7.4.2")])],"isStart":false});
            var Q3;
            Q3=makeQuery(id+"F2.opExtrude","CAP_EDGE",EDGE,{"disambiguationData":[OSD([sQuery(id+"F0.wireOp",EDGE,"E7.3.2")])],"isStart":false});
            var Q4;
            Q4=makeQuery(id+"F2.opExtrude","CAP_EDGE",EDGE,{"disambiguationData":[OSD([sQuery(id+"F0.wireOp",EDGE,"E2")])],"isStart":false});
            var Q5;
            Q5=makeQuery(id+"F2.opExtrude","CAP_EDGE",EDGE,{"disambiguationData":[OSD([sQuery(id+"F0.wireOp",EDGE,"E7.1.2")])],"isStart":false});
            var Q6;
            Q6=makeQuery(id+"F2.opExtrude","CAP_EDGE",EDGE,{"disambiguationData":[OSD([sQuery(id+"F0.wireOp",EDGE,"E7.2.2")])],"isStart":false});
            fillet(context, id + "F4", {"entities" : qUnion([Q0, Q1, Q2, Q3, Q4, Q5, Q6]), "radius" : .5 * mm, "tangentPropagation" : true, "allowEdgeOverflow" : false});
        }
    });
